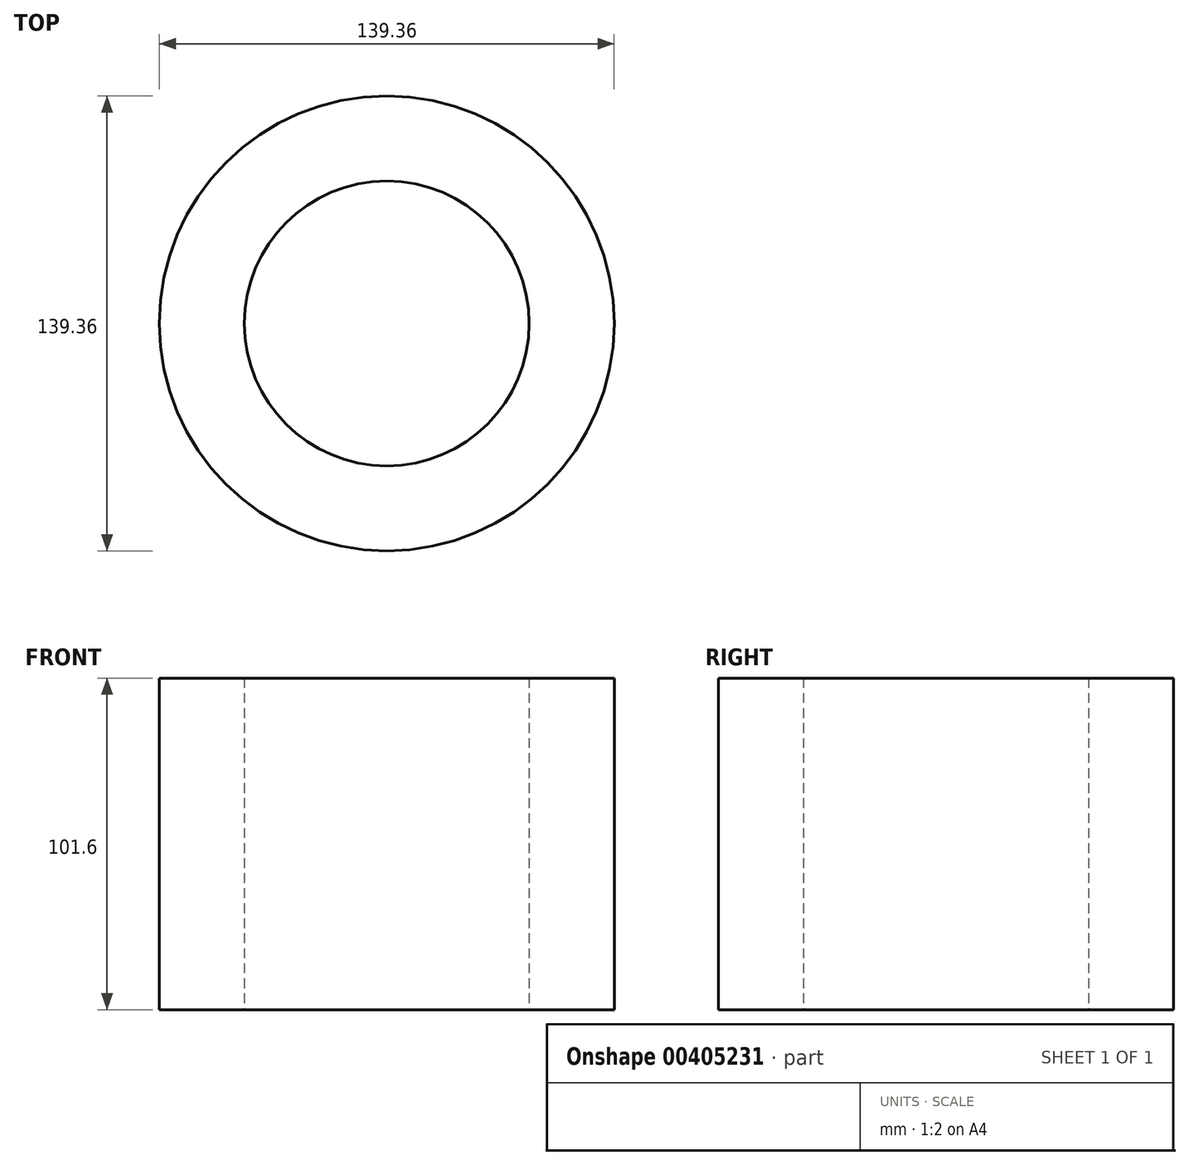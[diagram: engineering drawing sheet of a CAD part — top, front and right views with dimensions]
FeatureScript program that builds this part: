
annotation { "Feature Type Name" : "Feature", "Feature Type Description" : "" }
export const myFeature = defineFeature(function(context is Context, id is Id, definition is map)
    precondition{}
    {
        {
            var Q0;
            Q0=qCreatedBy(makeId("Top.planeOp"),FACE);
            var sketch = newSketch(context, id + "F0", { "sketchPlane" : qUnion([Q0])});
            skCircle(sketch, "E0", {"center": v(0, 0) * mm, "radius": 43.64 * mm});
            skCircle(sketch, "E1", {"center": v(0, 0) * mm, "radius": 69.68 * mm});
            skSolve(sketch);
        }
        {
            var Q0;
            Q0=makeQuery(id+"F0.imprint","IMPRINT",FACE,{"disambiguationData":[TD([[makeQuery(id+"F0.imprint","IMPRINT",EDGE,{"derivedFrom":sQuery(id+"F0.wireOp",EDGE,"E0")}),-1.0]])]});
            extrude(context, id + "F1", {"entities" : qUnion([Q0]), "depth" : 101.6 * mm});
        }
    });
